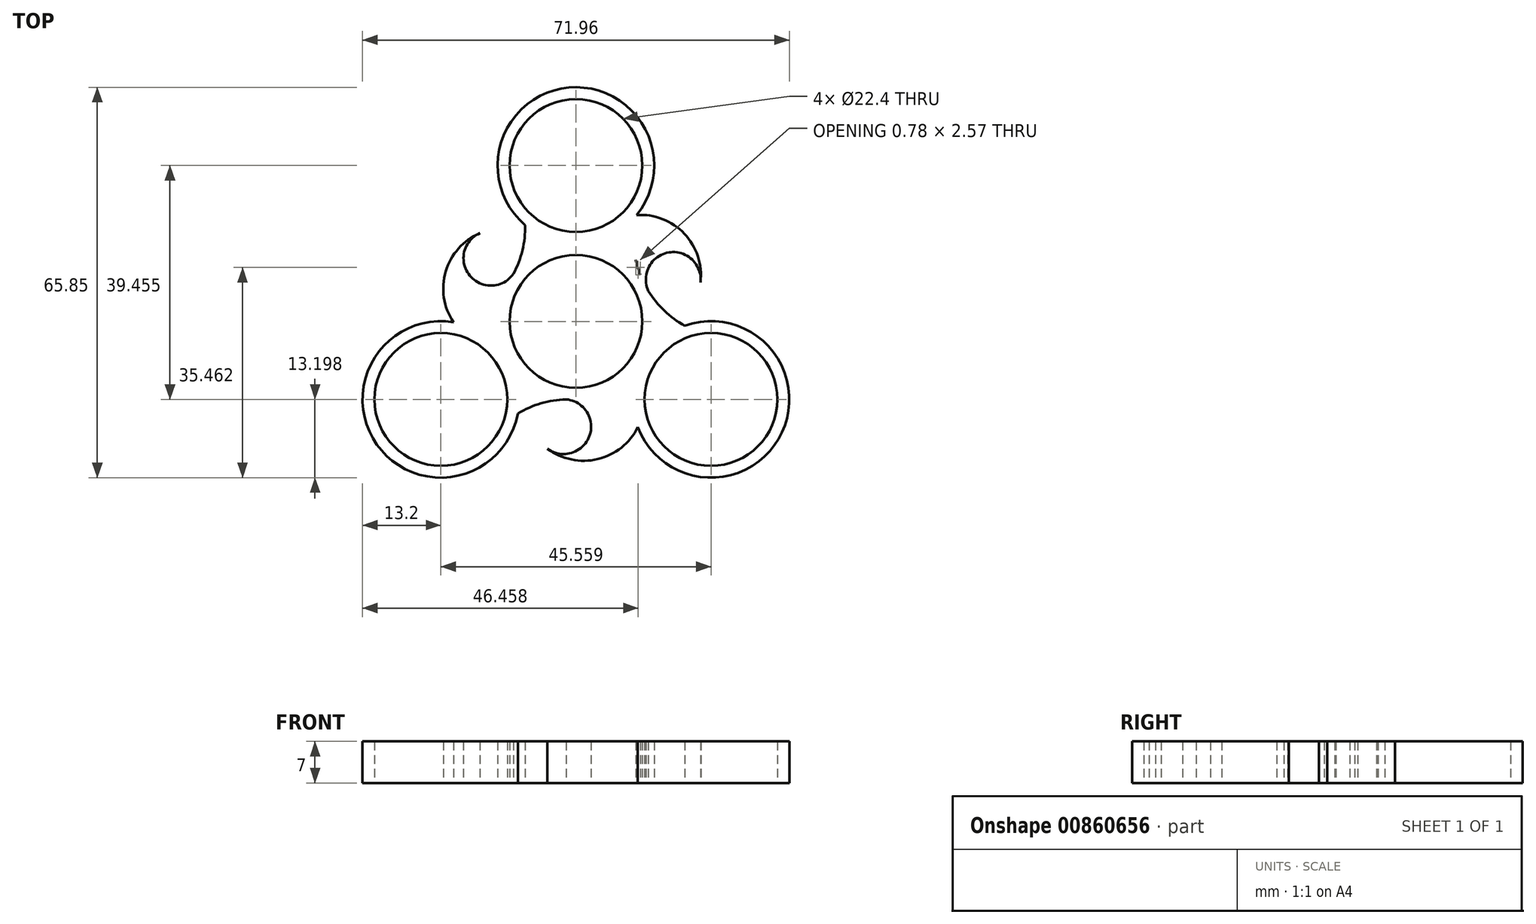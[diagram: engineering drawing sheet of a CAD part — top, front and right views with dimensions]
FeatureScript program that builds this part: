
annotation { "Feature Type Name" : "Feature", "Feature Type Description" : "" }
export const myFeature = defineFeature(function(context is Context, id is Id, definition is map)
    precondition{}
    {
        {
            var Q0;
            Q0=qCreatedBy(makeId("Top.planeOp"),FACE);
            var sketch = newSketch(context, id + "F0", { "sketchPlane" : qUnion([Q0])});
            skCircle(sketch, "E0", {"center": v(0, 0) * mm, "radius": 11.2 * mm});
            skCircle(sketch, "E1", {"center": v(0, 26.3) * mm, "radius": 11.2 * mm});
            skCircle(sketch, "E2", {"center": v(0, 26.3) * mm, "radius": 13.2 * mm});
            skCircle(sketch, "E3", {"center": v(0, 0) * mm, "radius": 13.2 * mm});
            skCircle(sketch, "E4.1.0", {"center": v(-22.78, -13.15) * mm, "radius": 11.2 * mm});
            skCircle(sketch, "E4.2.0", {"center": v(22.78, -13.15) * mm, "radius": 11.2 * mm});
            skCircle(sketch, "E5.1.0", {"center": v(-22.78, -13.15) * mm, "radius": 13.2 * mm});
            skCircle(sketch, "E5.2.0", {"center": v(22.78, -13.15) * mm, "radius": 13.2 * mm});
            skArc(sketch, "E6", {"start": v(10.16, 17.88) * mm, "mid": v(11.13, 7.2) * mm, "end": v(18.35, -0.72) * mm});
            skArc(sketch, "E7.1.0", {"start": v(-20.56, -0.14) * mm, "mid": v(-11.8, 6.04) * mm, "end": v(-8.55, 16.25) * mm});
            skArc(sketch, "E7.2.0", {"start": v(10.4, -17.74) * mm, "mid": v(0.67, -13.24) * mm, "end": v(-9.8, -15.53) * mm});
            skSolve(sketch);
        }
        {
            var Q0;
            {var subQ0=sQuery(id+"F0.wireOp",EDGE,"E6");var subQ1=sQuery(id+"F0.wireOp",EDGE,"E2");var subQ2=makeQuery(id+"F0.imprint","INTERSECT",VERTEX,{"derivedFrom":[subQ1,subQ0]});Q0=makeQuery(id+"F0.imprint","IMPRINT",FACE,{"disambiguationData":[TD([[makeQuery(id+"F0.imprint","IMPRINT",EDGE,{"disambiguationData":[TD([[subQ2,1.0]])],"derivedFrom":subQ1}),-1.0]])]});}
            var Q1;
            Q1=makeQuery(id+"F0.imprint","IMPRINT",FACE,{"disambiguationData":[TD([[makeQuery(id+"F0.imprint","IMPRINT",EDGE,{"derivedFrom":sQuery(id+"F0.wireOp",EDGE,"E1")}),-1.0]])]});
            var Q2;
            {var subQ0=sQuery(id+"F0.wireOp",EDGE,"E7.1.0");var subQ1=sQuery(id+"F0.wireOp",EDGE,"E2");var subQ2=makeQuery(id+"F0.imprint","INTERSECT",VERTEX,{"derivedFrom":[subQ1,subQ0]});Q2=makeQuery(id+"F0.imprint","IMPRINT",FACE,{"disambiguationData":[TD([[makeQuery(id+"F0.imprint","IMPRINT",EDGE,{"disambiguationData":[TD([[subQ2,-1.0]])],"derivedFrom":subQ1}),-1.0]])]});}
            var Q3;
            {var subQ0=sQuery(id+"F0.wireOp",EDGE,"E7.1.0");var subQ1=sQuery(id+"F0.wireOp",EDGE,"E3");var subQ2=makeQuery(id+"F0.imprint","INTERSECT",VERTEX,{"disambiguationData":[OD(1.0)],"derivedFrom":[subQ1,subQ0]});Q3=makeQuery(id+"F0.imprint","IMPRINT",FACE,{"disambiguationData":[TD([[makeQuery(id+"F0.imprint","IMPRINT",EDGE,{"disambiguationData":[TD([[subQ2,-1.0]])],"derivedFrom":subQ1}),-1.0]])]});}
            var Q4;
            {var subQ0=sQuery(id+"F0.wireOp",EDGE,"E7.2.0");var subQ1=sQuery(id+"F0.wireOp",EDGE,"E3");var subQ2=makeQuery(id+"F0.imprint","INTERSECT",VERTEX,{"disambiguationData":[OD(1.0)],"derivedFrom":[subQ1,subQ0]});Q4=makeQuery(id+"F0.imprint","IMPRINT",FACE,{"disambiguationData":[TD([[makeQuery(id+"F0.imprint","IMPRINT",EDGE,{"disambiguationData":[TD([[subQ2,-1.0]])],"derivedFrom":subQ1}),-1.0]])]});}
            var Q5;
            {var subQ0=sQuery(id+"F0.wireOp",EDGE,"E7.2.0");var subQ1=sQuery(id+"F0.wireOp",EDGE,"E3");var subQ2=makeQuery(id+"F0.imprint","INTERSECT",VERTEX,{"disambiguationData":[OD(0.0)],"derivedFrom":[subQ1,subQ0]});Q5=makeQuery(id+"F0.imprint","IMPRINT",FACE,{"disambiguationData":[TD([[makeQuery(id+"F0.imprint","IMPRINT",EDGE,{"disambiguationData":[TD([[subQ2,1.0]])],"derivedFrom":subQ1}),-1.0]])]});}
            var Q6;
            {var subQ0=sQuery(id+"F0.wireOp",EDGE,"E6");var subQ1=sQuery(id+"F0.wireOp",EDGE,"E3");var subQ2=makeQuery(id+"F0.imprint","INTERSECT",VERTEX,{"disambiguationData":[OD(1.0)],"derivedFrom":[subQ1,subQ0]});Q6=makeQuery(id+"F0.imprint","IMPRINT",FACE,{"disambiguationData":[TD([[makeQuery(id+"F0.imprint","IMPRINT",EDGE,{"disambiguationData":[TD([[subQ2,1.0]])],"derivedFrom":subQ1}),-1.0]])]});}
            var Q7;
            Q7=makeQuery(id+"F0.imprint","IMPRINT",FACE,{"disambiguationData":[TD([[makeQuery(id+"F0.imprint","IMPRINT",EDGE,{"derivedFrom":sQuery(id+"F0.wireOp",EDGE,"E4.2.0")}),-1.0]])]});
            var Q8;
            Q8=makeQuery(id+"F0.imprint","IMPRINT",FACE,{"disambiguationData":[TD([[makeQuery(id+"F0.imprint","IMPRINT",EDGE,{"derivedFrom":sQuery(id+"F0.wireOp",EDGE,"E4.1.0")}),-1.0]])]});
            var Q9;
            Q9=makeQuery(id+"F0.imprint","IMPRINT",FACE,{"disambiguationData":[TD([[makeQuery(id+"F0.imprint","IMPRINT",EDGE,{"derivedFrom":sQuery(id+"F0.wireOp",EDGE,"E0")}),-1.0]])]});
            var Q10;
            {var subQ0=sQuery(id+"F0.wireOp",EDGE,"E3");var subQ1=sQuery(id+"F0.wireOp",EDGE,"E2");var subQ2=makeQuery(id+"F0.imprint","INTERSECT",VERTEX,{"disambiguationData":[OD(0.0)],"derivedFrom":[subQ1,subQ0]});Q10=makeQuery(id+"F0.imprint","IMPRINT",FACE,{"disambiguationData":[TD([[makeQuery(id+"F0.imprint","IMPRINT",EDGE,{"disambiguationData":[TD([[subQ2,-1.0]])],"derivedFrom":subQ1}),1.0]])]});}
            var Q11;
            {var subQ0=sQuery(id+"F0.wireOp",EDGE,"E5.1.0");var subQ1=sQuery(id+"F0.wireOp",EDGE,"E3");var subQ2=makeQuery(id+"F0.imprint","INTERSECT",VERTEX,{"disambiguationData":[OD(0.0)],"derivedFrom":[subQ1,subQ0]});Q11=makeQuery(id+"F0.imprint","IMPRINT",FACE,{"disambiguationData":[TD([[makeQuery(id+"F0.imprint","IMPRINT",EDGE,{"disambiguationData":[TD([[subQ2,-1.0]])],"derivedFrom":subQ1}),1.0]])]});}
            var Q12;
            {var subQ0=sQuery(id+"F0.wireOp",EDGE,"E5.2.0");var subQ1=sQuery(id+"F0.wireOp",EDGE,"E3");var subQ2=makeQuery(id+"F0.imprint","INTERSECT",VERTEX,{"disambiguationData":[OD(0.0)],"derivedFrom":[subQ1,subQ0]});Q12=makeQuery(id+"F0.imprint","IMPRINT",FACE,{"disambiguationData":[TD([[makeQuery(id+"F0.imprint","IMPRINT",EDGE,{"disambiguationData":[TD([[subQ2,-1.0]])],"derivedFrom":subQ1}),1.0]])]});}
            extrude(context, id + "F1", {"entities" : qUnion([Q0, Q1, Q2, Q3, Q4, Q5, Q6, Q7, Q8, Q9, Q10, Q11, Q12]), "depth" : 7 * mm, "offsetDistance" : 25 * mm});
        }
        {
            var Q0;
            Q0=qCreatedBy(makeId("Top.planeOp"),FACE);
            var sketch = newSketch(context, id + "F2", { "sketchPlane" : qUnion([Q0])});
            skArc(sketch, "E8", {"start": v(21, 6.58) * mm, "mid": v(18.24, 14.84) * mm, "end": v(10.1, 17.95) * mm});
            skArc(sketch, "E9", {"start": v(21, 6.58) * mm, "mid": v(15.57, 11.63) * mm, "end": v(12.3, 4.98) * mm});
            skArc(sketch, "E10.1.0", {"start": v(-16.2, 14.9) * mm, "mid": v(-21.97, 8.37) * mm, "end": v(-20.6, -0.23) * mm});
            skArc(sketch, "E10.2.0", {"start": v(-4.8, -21.48) * mm, "mid": v(3.74, -23.21) * mm, "end": v(10.5, -17.72) * mm});
            skPoint(sketch, "E10.center", {"position": v(0, 0) * mm});
            skArc(sketch, "E11.1.0", {"start": v(-16.2, 14.9) * mm, "mid": v(-17.85, 7.67) * mm, "end": v(-10.46, 8.16) * mm});
            skArc(sketch, "E11.2.0", {"start": v(-4.8, -21.48) * mm, "mid": v(2.28, -19.3) * mm, "end": v(-1.84, -13.13) * mm});
            skArc(sketch, "E12", {"start": v(10.1, 17.95) * mm, "mid": v(9.92, 11.25) * mm, "end": v(12.3, 4.98) * mm});
            skArc(sketch, "E13", {"start": v(-20.6, -0.23) * mm, "mid": v(-14.68, 2.94) * mm, "end": v(-10.46, 8.16) * mm});
            skArc(sketch, "E14", {"start": v(10.5, -17.72) * mm, "mid": v(4.79, -14.2) * mm, "end": v(-1.84, -13.13) * mm});
            skSolve(sketch);
        }
        {
            var Q0;
            Q0=makeQuery(id+"F2.imprint","IMPRINT",FACE,{"disambiguationData":[TD([[makeQuery(id+"F2.imprint","IMPRINT",EDGE,{"derivedFrom":sQuery(id+"F2.wireOp",EDGE,"E8")}),1.0]])]});
            var Q1;
            Q1=makeQuery(id+"F2.imprint","IMPRINT",FACE,{"disambiguationData":[TD([[makeQuery(id+"F2.imprint","IMPRINT",EDGE,{"derivedFrom":sQuery(id+"F2.wireOp",EDGE,"E10.2.0")}),1.0]])]});
            var Q2;
            Q2=makeQuery(id+"F2.imprint","IMPRINT",FACE,{"disambiguationData":[TD([[makeQuery(id+"F2.imprint","IMPRINT",EDGE,{"derivedFrom":sQuery(id+"F2.wireOp",EDGE,"E10.1.0")}),1.0]])]});
            extrude(context, id + "F3", {"entities" : qUnion([Q0, Q1, Q2]), "operationType" : NewBodyOperationType.ADD, "depth" : 7 * mm, "offsetDistance" : 25 * mm});
        }
    });
